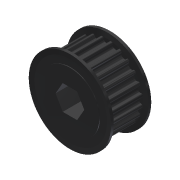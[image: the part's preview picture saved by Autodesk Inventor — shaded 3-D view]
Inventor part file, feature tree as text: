
AUTODESK INVENTOR PART (.ipt)
format: ipt  version: 2013 (Build 170138000, 138)  size: 703,488 bytes
history: native  units: in
note: dims shown in document units (in); Inventor stores cm internally (conversion verified against a paired STEP export)
features: mirror x1, other x1, imported_body x1
ambient origin geometry x8: Origin, YZ Plane, XZ Plane, XY Plane, X Axis, Y Axis, Z Axis, Center Point
feature tree (3):
  mirror  "Mirror1"
  other  "217-3228-STEP1"
  imported_body  "Base1"
